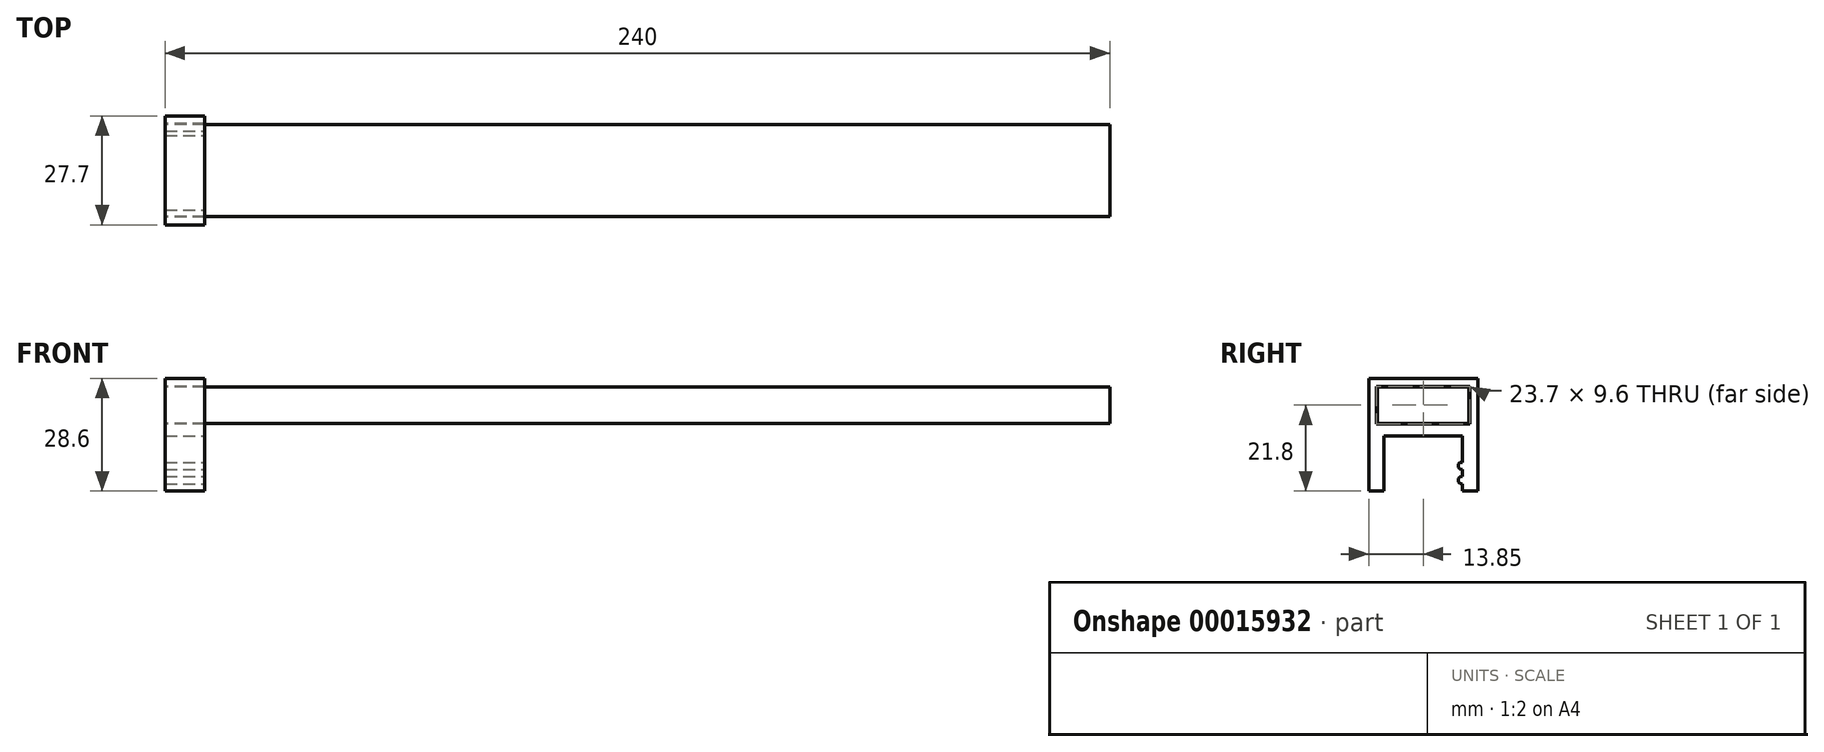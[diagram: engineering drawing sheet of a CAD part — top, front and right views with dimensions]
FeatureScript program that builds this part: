
annotation { "Feature Type Name" : "Feature", "Feature Type Description" : "" }
export const myFeature = defineFeature(function(context is Context, id is Id, definition is map)
    precondition{}
    {
        {
            var Q0;
            Q0=qCreatedBy(makeId("Right.planeOp"),FACE);
            var sketch = newSketch(context, id + "F0", { "sketchPlane" : qUnion([Q0])});
            skLineSegment(sketch, "E0.bottom", {"start": v(-23.3, 9.2) * mm, "end": v(0, 9.2) * mm});
            skLineSegment(sketch, "E0.top", {"start": v(-23.3, 0) * mm, "end": v(0, 0) * mm});
            skLineSegment(sketch, "E0.left", {"start": v(-23.3, 9.2) * mm, "end": v(-23.3, 0) * mm});
            skLineSegment(sketch, "E0.right", {"start": v(0, 9.2) * mm, "end": v(0, 0) * mm});
            skSolve(sketch);
        }
        {
            var Q0;
            Q0 = qSketchRegion(id + "F0", true);
            extrude(context, id + "F1", {"entities" : qUnion([Q0]), "depth" : 240 * mm});
        }
        {
            var Q0;
            Q0=makeQuery(id+"F1.opExtrude","CAP_FACE",FACE,{"disambiguationData":[OSD([sQuery(id+"F0.wireOp",EDGE,"E0.bottom"),sQuery(id+"F0.wireOp",EDGE,"E0.top"),sQuery(id+"F0.wireOp",EDGE,"E0.left"),sQuery(id+"F0.wireOp",EDGE,"E0.right")])],"isStart":true});
            var sketch = newSketch(context, id + "F2", { "sketchPlane" : qUnion([Q0])});
            skLineSegment(sketch, "E1.bottom", {"start": v(-2.2, 11.4) * mm, "end": v(25.5, 11.4) * mm});
            skLineSegment(sketch, "E1.top", {"start": v(-2.2, -3.2) * mm, "end": v(25.5, -3.2) * mm});
            skLineSegment(sketch, "E1.left", {"start": v(-2.2, 11.4) * mm, "end": v(-2.2, -3.2) * mm});
            skLineSegment(sketch, "E1.right", {"start": v(25.5, 11.4) * mm, "end": v(25.5, -3.2) * mm});
            skLineSegment(sketch, "E2.bottom", {"start": v(-0.2, 9.4) * mm, "end": v(23.5, 9.4) * mm});
            skLineSegment(sketch, "E2.top", {"start": v(-0.2, -0.2) * mm, "end": v(23.5, -0.2) * mm});
            skLineSegment(sketch, "E2.left", {"start": v(-0.2, 9.4) * mm, "end": v(-0.2, -0.2) * mm});
            skLineSegment(sketch, "E2.right", {"start": v(23.5, 9.4) * mm, "end": v(23.5, -0.2) * mm});
            skSolve(sketch);
        }
        {
            var Q0;
            Q0 = qSketchRegion(id + "F2", true);
            extrude(context, id + "F3", {"entities" : qUnion([Q0]), "oppositeDirection" : true, "depth" : 10 * mm});
        }
        {
            var Q0;
            Q0=makeQuery(id+"F3.opExtrude","SWEPT_FACE",FACE,{"disambiguationData":[OSD([sQuery(id+"F2.wireOp",EDGE,"E1.top")])]});
            var sketch = newSketch(context, id + "F4", { "sketchPlane" : qUnion([Q0])});
            skLineSegment(sketch, "E3.bottom", {"start": v(0, 25.5) * mm, "end": v(10, 25.5) * mm});
            skLineSegment(sketch, "E3.top", {"start": v(0, 21.65) * mm, "end": v(10, 21.65) * mm});
            skLineSegment(sketch, "E3.left", {"start": v(0, 25.5) * mm, "end": v(0, 21.65) * mm});
            skLineSegment(sketch, "E3.right", {"start": v(10, 25.5) * mm, "end": v(10, 21.65) * mm});
            skLineSegment(sketch, "E4.bottom", {"start": v(0, -2.2) * mm, "end": v(10, -2.2) * mm});
            skLineSegment(sketch, "E4.top", {"start": v(0, 1.65) * mm, "end": v(10, 1.65) * mm});
            skLineSegment(sketch, "E4.left", {"start": v(0, -2.2) * mm, "end": v(0, 1.65) * mm});
            skLineSegment(sketch, "E4.right", {"start": v(10, -2.2) * mm, "end": v(10, 1.65) * mm});
            skSolve(sketch);
        }
        {
            var Q0;
            Q0 = qSketchRegion(id + "F4", true);
            extrude(context, id + "F5", {"entities" : qUnion([Q0]), "operationType" : NewBodyOperationType.ADD, "depth" : 14 * mm});
        }
        {
            var Q0;
            Q0=makeQuery(id+"F5.opExtrude","SWEPT_FACE",FACE,{"disambiguationData":[OSD([sQuery(id+"F4.wireOp",EDGE,"E4.top")])]});
            var sketch = newSketch(context, id + "F6", { "sketchPlane" : qUnion([Q0])});
            skLineSegment(sketch, "E5.bottom", {"start": v(0, -9.9) * mm, "end": v(10, -9.9) * mm});
            skLineSegment(sketch, "E5.top", {"start": v(0, -11.7) * mm, "end": v(10, -11.7) * mm});
            skLineSegment(sketch, "E5.left", {"start": v(0, -9.9) * mm, "end": v(0, -11.7) * mm});
            skLineSegment(sketch, "E5.right", {"start": v(10, -9.9) * mm, "end": v(10, -11.7) * mm});
            skLineSegment(sketch, "E6.bottom", {"start": v(0, -13.55) * mm, "end": v(10, -13.55) * mm});
            skLineSegment(sketch, "E6.top", {"start": v(0, -15.35) * mm, "end": v(10, -15.35) * mm});
            skLineSegment(sketch, "E6.left", {"start": v(0, -13.55) * mm, "end": v(0, -15.35) * mm});
            skLineSegment(sketch, "E6.right", {"start": v(10, -13.55) * mm, "end": v(10, -15.35) * mm});
            skSolve(sketch);
        }
        {
            var Q0;
            Q0 = qSketchRegion(id + "F6", true);
            extrude(context, id + "F7", {"entities" : qUnion([Q0]), "operationType" : NewBodyOperationType.ADD, "offsetDistance" : 25 * mm, "depth" : 1.1 * mm});
        }
        {
            var Q0;
            Q0=makeQuery(id+"F7.opExtrude","CAP_EDGE",EDGE,{"disambiguationData":[OSD([sQuery(id+"F6.wireOp",EDGE,"E5.bottom")])],"isStart":false});
            var Q1;
            Q1=makeQuery(id+"F7.opExtrude","CAP_EDGE",EDGE,{"disambiguationData":[OSD([sQuery(id+"F6.wireOp",EDGE,"E5.top")])],"isStart":false});
            var Q2;
            Q2=makeQuery(id+"F7.opExtrude","CAP_EDGE",EDGE,{"disambiguationData":[OSD([sQuery(id+"F6.wireOp",EDGE,"E6.bottom")])],"isStart":false});
            var Q3;
            Q3=makeQuery(id+"F7.opExtrude","CAP_EDGE",EDGE,{"disambiguationData":[OSD([sQuery(id+"F6.wireOp",EDGE,"E6.top")])],"isStart":false});
            fillet(context, id + "F8", {"entities" : qUnion([Q0, Q1, Q2, Q3]), "radius" : 0.8 * mm, "tangentPropagation" : true, "defaultsChanged" : false, "vertexSettings" : [], "allowEdgeOverflow" : false});
        }
    });
